# Revit family: Haworth_Cappellini_Bac_Table_Rectangle_EU_PRELIMINARY
name_source: partatom
category: Furniture
revit_build: Autodesk Revit 2018 (Build: 20170223_1515(x64)
units: mm (PartAtom-declared; Revit-internal decimal feet)

## family parameters
Always vertical = Yes
Cut with Voids When Loaded = No
OmniClass Number = 23.40.70.14.64.21
OmniClass Title = Systems Furniture
Room Calculation Point = No
Shared = No
Work Plane-Based = No

## types (2) — shared parameters
Actual Depth = 85 cm
Actual Height = 74 cm
Assembly Code = E2020200
Description = Haworth - Cappellini - Bac - Table - Rectangle
Leg Depth = 10 cm
Manufacturer = Haworth
Model = BACX
Revision Number = 4
Size = Verify Final Dim. w/ Haworth
Support Depth = 6 cm
Support Height = 11 cm
Support Offset = 20 cm
Table Thickness = 3 cm
URL = https://www.haworth.com
URL - Product = https://www.haworth.com
Warranty = http://www.haworth.com

## per-type parameters (varying)
| type | Actual Width | Large | Small |
| Small Table | 200 cm | No | Yes |
| Large Table | 240 cm | Yes | No |

## geometry (parser evidence)
native form markers: Sweep x2
no freeform markers — native parametric forms only
